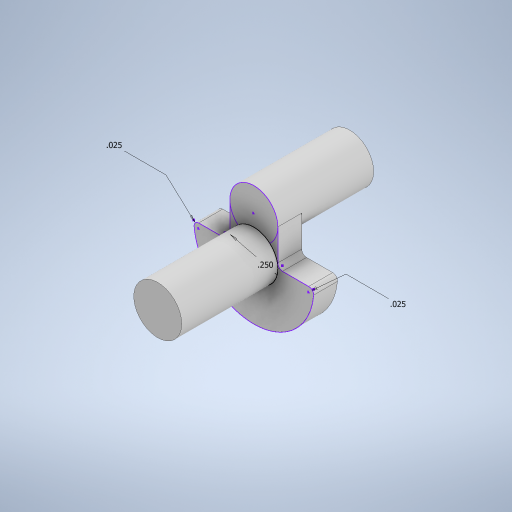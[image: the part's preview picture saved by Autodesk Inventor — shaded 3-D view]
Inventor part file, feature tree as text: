
AUTODESK INVENTOR PART (.ipt)
format: ipt  version: 2023 (Build 270158000, 158)  size: 269,824 bytes
history: native  units: in
note: dims shown in document units (in); Inventor stores cm internally (conversion verified against a paired STEP export)
features: extrude x3, sketch x1
ambient origin geometry x8: Origin, YZ Plane, XZ Plane, XY Plane, X Axis, Y Axis, Z Axis, Center Point
bodies: Solid1 (feature_tree)
feature tree (4):
  sketch  "Sketch1"  dims[d2=0.025in d3=0.025in d4=0.25in d5=0.5in d6=0.0in d7=0.125in d8=0.0in d9=0.5in d10=0.0in]
  extrude  "Extrusion1"  Depth=0.025in
  extrude  "Extrusion2"  Depth=0.25in
  extrude  "Extrusion3"  Depth=0.5in TaperAngle=0.0deg
